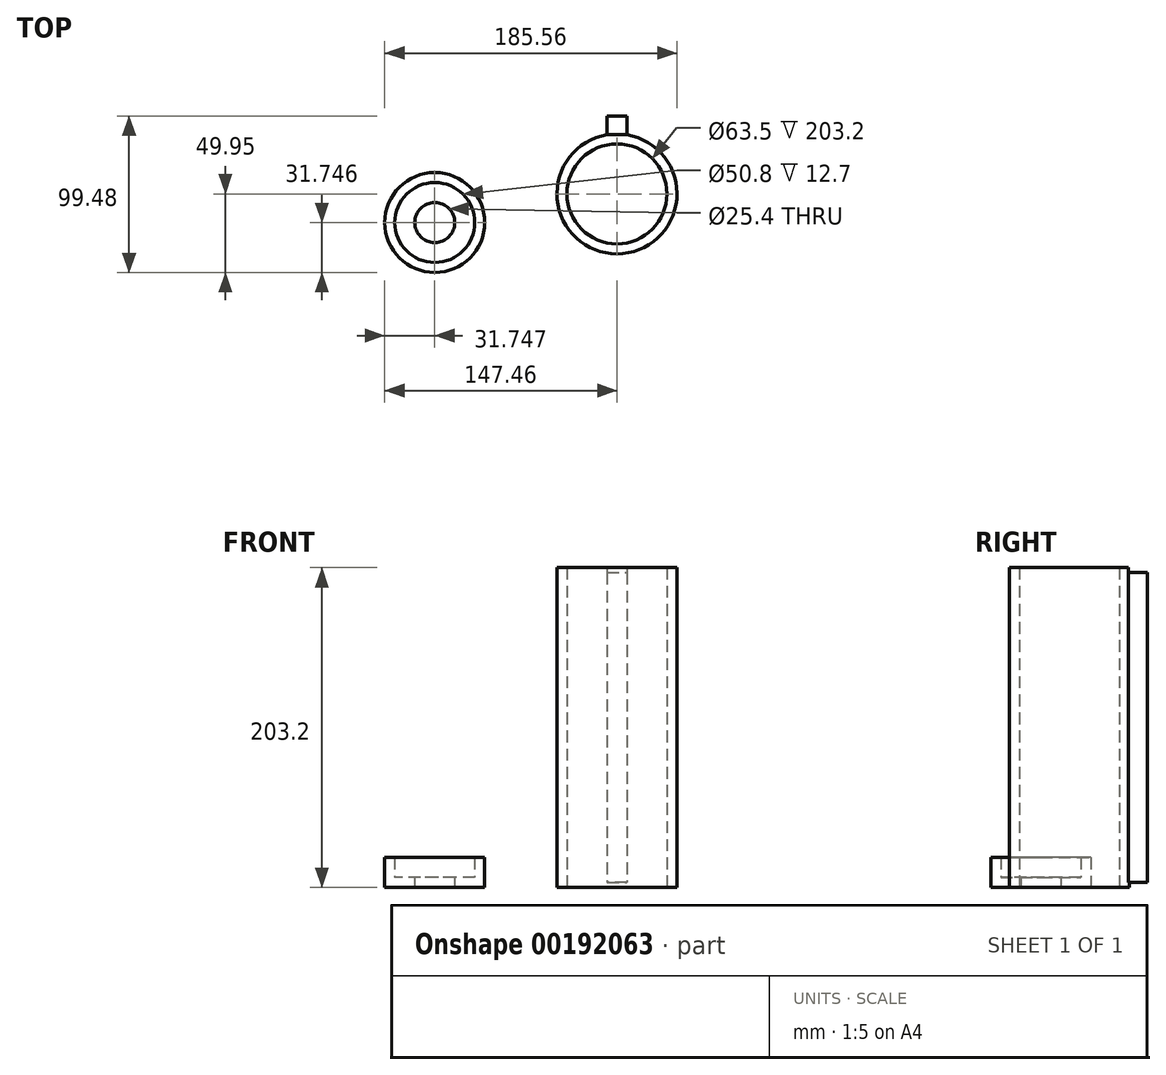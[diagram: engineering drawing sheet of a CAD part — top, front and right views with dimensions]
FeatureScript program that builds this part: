
annotation { "Feature Type Name" : "Feature", "Feature Type Description" : "" }
export const myFeature = defineFeature(function(context is Context, id is Id, definition is map)
    precondition{}
    {
        {
            var Q0;
            Q0=qCreatedBy(makeId("Top.planeOp"),FACE);
            var sketch = newSketch(context, id + "F0", { "sketchPlane" : qUnion([Q0])});
            skCircle(sketch, "E0", {"center": v(0, 0) * mm, "radius": 31.75 * mm});
            skCircle(sketch, "E1", {"center": v(0, 0) * mm, "radius": 38.1 * mm});
            skCircle(sketch, "E2", {"center": v(-115.71, -18.2) * mm, "radius": 12.7 * mm});
            skCircle(sketch, "E3", {"center": v(-115.71, -18.2) * mm, "radius": 31.75 * mm});
            skCircle(sketch, "E4", {"center": v(-115.71, -18.2) * mm, "radius": 25.4 * mm});
            skLineSegment(sketch, "E5", {"start": v(0, 38.1) * mm, "end": v(0, 49.53) * mm});
            skLineSegment(sketch, "E6", {"start": v(0, 49.53) * mm, "end": v(6.35, 49.53) * mm});
            skLineSegment(sketch, "E7", {"start": v(6.35, 49.53) * mm, "end": v(6.35, 37.57) * mm});
            skLineSegment(sketch, "E8", {"start": v(0, 49.53) * mm, "end": v(-6.35, 49.53) * mm});
            skLineSegment(sketch, "E9", {"start": v(-6.35, 49.53) * mm, "end": v(-6.35, 37.57) * mm});
            skSolve(sketch);
        }
        {
            var Q0;
            Q0=makeQuery(id+"F0.imprint","IMPRINT",FACE,{"disambiguationData":[TD([[makeQuery(id+"F0.imprint","IMPRINT",EDGE,{"derivedFrom":sQuery(id+"F0.wireOp",EDGE,"zd0O7Sh5-Xt7p-uVyE-hd8E-lKO0Mg8OgbEY")}),1.0]])]});
            var Q1;
            Q1=makeQuery(id+"F0.imprint","IMPRINT",FACE,{"disambiguationData":[TD([[makeQuery(id+"F0.imprint","IMPRINT",EDGE,{"derivedFrom":sQuery(id+"F0.wireOp",EDGE,"E3")}),1.0]])]});
            extrude(context, id + "F1", {"entities" : qUnion([Q0, Q1]), "depth" : 19.05 * mm});
        }
        {
            var Q0;
            Q0=makeQuery(id+"F0.imprint","IMPRINT",FACE,{"disambiguationData":[TD([[makeQuery(id+"F0.imprint","IMPRINT",EDGE,{"derivedFrom":sQuery(id+"F0.wireOp",EDGE,"E2")}),-1.0]])]});
            extrude(context, id + "F2", {"entities" : qUnion([Q0]), "operationType" : NewBodyOperationType.ADD, "depth" : 6.35 * mm});
        }
        {
            var Q0;
            Q0=makeQuery(id+"F0.imprint","IMPRINT",FACE,{"disambiguationData":[TD([[makeQuery(id+"F0.imprint","IMPRINT",EDGE,{"derivedFrom":sQuery(id+"F0.wireOp",EDGE,"E0")}),-1.0]])]});
            var Q1;
            {var subQ0=sQuery(id+"F0.wireOp",EDGE,"E5");Q1=makeQuery(id+"F0.imprint","IMPRINT",FACE,{"disambiguationData":[TD([[makeQuery(id+"F0.imprint","IMPRINT",EDGE,{"derivedFrom":subQ0}),-1.0]])]});}
            var Q2;
            {var subQ0=sQuery(id+"F0.wireOp",EDGE,"E5");Q2=makeQuery(id+"F0.imprint","IMPRINT",FACE,{"disambiguationData":[TD([[makeQuery(id+"F0.imprint","IMPRINT",EDGE,{"derivedFrom":subQ0}),1.0]])]});}
            extrude(context, id + "F3", {"entities" : qUnion([Q0, Q1, Q2]), "depth" : 203.2 * mm});
        }
        {
            var Q0;
            Q0=makeQuery(id+"F3.opExtrude","CAP_FACE",FACE,{"disambiguationData":[OSD([sQuery(id+"F0.wireOp",EDGE,"E0"),sQuery(id+"F0.wireOp",EDGE,"E1"),sQuery(id+"F0.wireOp",EDGE,"E6"),sQuery(id+"F0.wireOp",EDGE,"E7"),sQuery(id+"F0.wireOp",EDGE,"E8"),sQuery(id+"F0.wireOp",EDGE,"E9")])],"isStart":false});
            var sketch = newSketch(context, id + "F4", { "sketchPlane" : qUnion([Q0])});
            skLineSegment(sketch, "E10.bottom", {"start": v(-6.35, 37.57) * mm, "end": v(6.35, 37.57) * mm});
            skLineSegment(sketch, "E10.top", {"start": v(-6.35, 49.53) * mm, "end": v(6.35, 49.53) * mm});
            skLineSegment(sketch, "E10.left", {"start": v(-6.35, 37.57) * mm, "end": v(-6.35, 49.53) * mm});
            skLineSegment(sketch, "E10.right", {"start": v(6.35, 37.57) * mm, "end": v(6.35, 49.53) * mm});
            skSolve(sketch);
        }
        {
            var Q0;
            Q0=makeQuery(id+"F4.imprint","IMPRINT",FACE,{"disambiguationData":[TD([[makeQuery(id+"F4.imprint","IMPRINT",EDGE,{"derivedFrom":sQuery(id+"F4.wireOp",EDGE,"E10.bottom")}),1.0]])]});
            extrude(context, id + "F5", {"entities" : qUnion([Q0]), "operationType" : NewBodyOperationType.REMOVE, "oppositeDirection" : true, "depth" : 3.17 * mm});
        }
        {
            var Q0;
            {var subQ0=sQuery(id+"F0.wireOp",EDGE,"E5");Q0=makeQuery(id+"F0.imprint","IMPRINT",FACE,{"disambiguationData":[TD([[makeQuery(id+"F0.imprint","IMPRINT",EDGE,{"derivedFrom":subQ0}),-1.0]])]});}
            var Q1;
            {var subQ0=sQuery(id+"F0.wireOp",EDGE,"E5");Q1=makeQuery(id+"F0.imprint","IMPRINT",FACE,{"disambiguationData":[TD([[makeQuery(id+"F0.imprint","IMPRINT",EDGE,{"derivedFrom":subQ0}),1.0]])]});}
            extrude(context, id + "F6", {"entities" : qUnion([Q0, Q1]), "operationType" : NewBodyOperationType.REMOVE, "depth" : 3.17 * mm});
        }
    });
